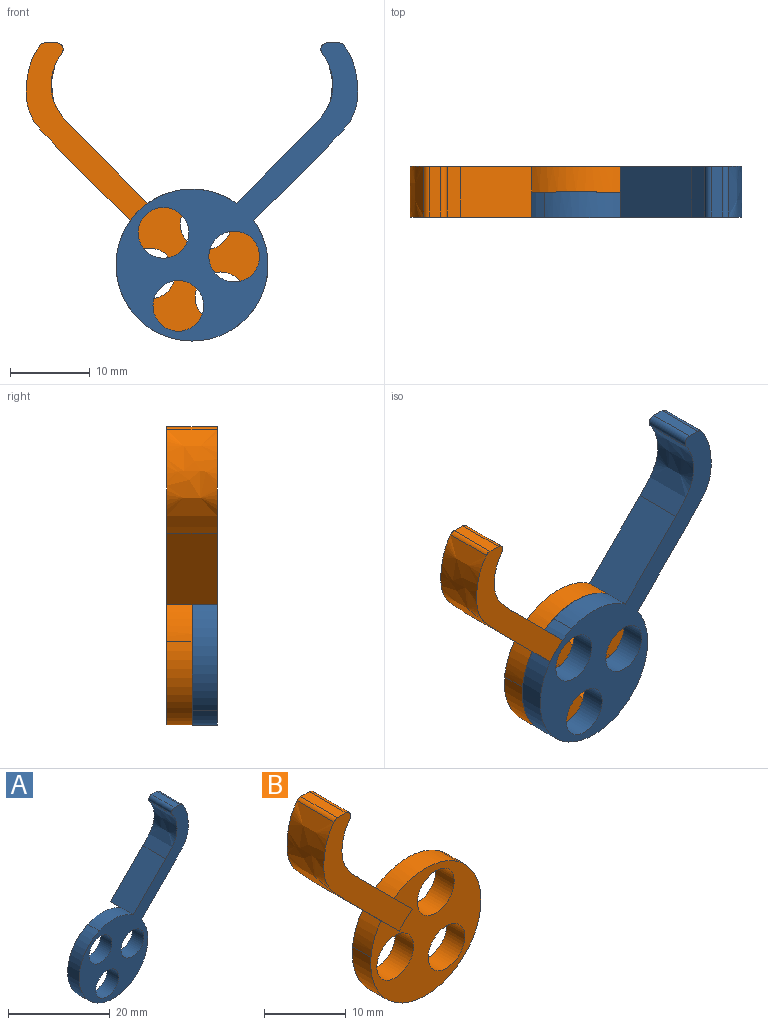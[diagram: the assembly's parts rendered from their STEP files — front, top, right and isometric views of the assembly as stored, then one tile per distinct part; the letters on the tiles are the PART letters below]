
ASSEMBLY  parts=2 mates=1
PART A: 18 faces, bbox 30.4x6.4x37.4 mm
  f0: cylinder r=9.53mm len=6.47mm, axis (0,1,0), area 21.7mm2, adj f2,f7,f8,f11
  f1: cylinder r=9.53mm len=16.42mm, axis (0,1,0), area 63.3mm2, adj f2,f6,f7,f8
  f2: cylinder r=9.53mm len=15.02mm, axis (0,1,0), area 63.3mm2, adj f0,f1,f7,f8
  f3: cylinder r=3.17mm len=6.35mm, axis (0,1,0), area 63.3mm2, adj f7,f8
  f4: cylinder r=3.17mm len=6.35mm, axis (0,1,0), area 63.3mm2, adj f7,f8
  f5: cylinder r=3.17mm len=6.35mm, axis (0,1,0), area 63.3mm2, adj f7,f8
  f6: cylinder r=9.53mm len=9.48mm, axis (0,1,0), area 31.7mm2, adj f1,f7,f8,f9
  f7: plane 37.37x30.44mm, normal (0,-1,0), area 271.6mm2, adj f0,f1,f2,f3,f4,f5,f6,f9
  f8: plane 19.05x19.05mm, normal (0,1,0), area 190mm2, adj f0,f1,f2,f3,f4,f5,f6,f10
  f9: plane 8.98x8.98mm, normal (-0.71,0,0.71), area 80.6mm2, adj f6,f7,f10,f14,f15
  f10: cylinder r=9.53mm len=3.18mm, axis (0,1,0), area 9.9mm2, adj f8,f9,f11,f15
  f11: plane 8.98x8.98mm, normal (0.71,0,-0.71), area 80.6mm2, adj f0,f7,f10,f12,f15
  f12: extruded ~13x6.35mm, area 93.5mm2, adj f7,f11,f15,f17
  f13: plane 6.35x1.48mm, normal (0,0,1), area 9.4mm2, adj f7,f15,f16,f17
  f14: extruded ~9.85x6.35mm, area 70.8mm2, adj f7,f9,f15,f16
  f15: plane 22.3x15.37mm, normal (0,1,0), area 81.6mm2, adj f9,f10,f11,f12,f13,f14,f16,f17
  f16: cylinder r=0.79mm len=6.35mm, axis (0,1,0), area 11.1mm2, adj f7,f13,f14,f15
  f17: cylinder r=0.79mm len=6.35mm, axis (0,1,0), area 4.6mm2, adj f7,f12,f13,f15
PART B: 18 faces, bbox 30.4x6.4x37.4 mm
  f0: cylinder r=9.53mm len=4.62mm, axis (0,-1,0), area 15.8mm2, adj f1,f7,f8,f14
  f1: cylinder r=9.53mm len=13.46mm, axis (0,-1,0), area 63.3mm2, adj f0,f2,f7,f8
  f2: cylinder r=9.53mm len=16.42mm, axis (0,-1,0), area 63.3mm2, adj f1,f6,f7,f8
  f3: cylinder r=3.17mm len=6.35mm, axis (0,-1,0), area 63.3mm2, adj f7,f8
  f4: cylinder r=3.17mm len=6.35mm, axis (0,-1,0), area 63.3mm2, adj f7,f8
  f5: cylinder r=3.17mm len=6.35mm, axis (0,-1,0), area 63.3mm2, adj f7,f8
  f6: cylinder r=9.53mm len=11.08mm, axis (0,-1,0), area 37.6mm2, adj f2,f7,f8,f10
  f7: plane 37.37x30.44mm, normal (0,1,0), area 271.6mm2, adj f0,f1,f2,f3,f4,f5,f6,f10
  f8: plane 19.05x19.05mm, normal (0,-1,0), area 190mm2, adj f0,f1,f2,f3,f4,f5,f6,f9
  f9: cylinder r=9.53mm len=3.18mm, axis (0,1,0), area 9.9mm2, adj f8,f10,f14,f15
  f10: plane 8.98x8.98mm, normal (0.71,0,0.71), area 80.6mm2, adj f6,f7,f9,f11,f15
  f11: extruded ~9.85x6.35mm, area 70.8mm2, adj f7,f10,f15,f16
  f12: plane 6.35x1.48mm, normal (0,0,1), area 9.4mm2, adj f7,f15,f16,f17
  f13: extruded ~13x6.35mm, area 93.5mm2, adj f7,f14,f15,f17
  f14: plane 8.98x8.98mm, normal (-0.71,0,-0.71), area 80.6mm2, adj f0,f7,f9,f13,f15
  f15: plane 22.3x15.37mm, normal (0,-1,0), area 81.6mm2, adj f9,f10,f11,f12,f13,f14,f16,f17
  f16: cylinder r=0.79mm len=6.35mm, axis (0,1,0), area 11.1mm2, adj f7,f11,f12,f15
  f17: cylinder r=0.79mm len=6.35mm, axis (0,1,0), area 4.6mm2, adj f7,f12,f13,f15
PLACE A t=(-9.31,0,-0.63)mm
PLACE B t=(-9.31,0,-0.63)mm
MATE revolute B.f0 <-> A.f2  axis (0,-1,0) through (-9.31,0,-0.63)mm
